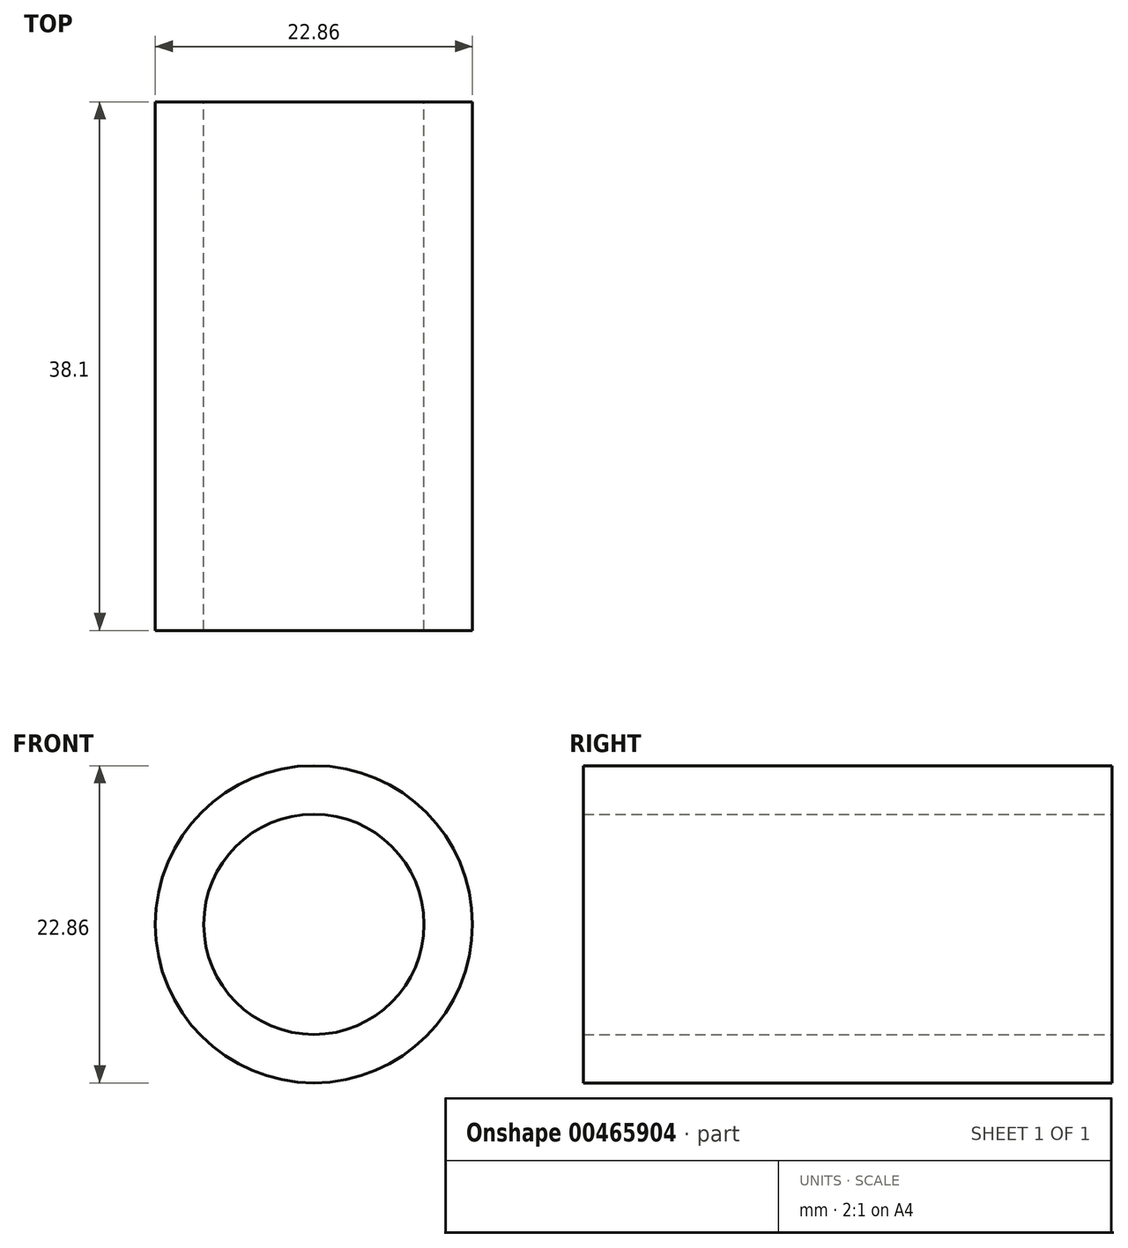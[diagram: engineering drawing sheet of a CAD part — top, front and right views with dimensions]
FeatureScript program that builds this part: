
annotation { "Feature Type Name" : "Feature", "Feature Type Description" : "" }
export const myFeature = defineFeature(function(context is Context, id is Id, definition is map)
    precondition{}
    {
        {
            var Q0;
            Q0=qCreatedBy(makeId("Front.planeOp"),FACE);
            var sketch = newSketch(context, id + "F0", { "sketchPlane" : qUnion([Q0])});
            skCircle(sketch, "E0", {"center": v(0, 0) * mm, "radius": 7.94 * mm});
            skCircle(sketch, "E1", {"center": v(0, 0) * mm, "radius": 11.43 * mm});
            skSolve(sketch);
        }
        {
            var Q0;
            Q0=makeQuery(id+"F0.imprint","IMPRINT",FACE,{"disambiguationData":[TD([[makeQuery(id+"F0.imprint","IMPRINT",EDGE,{"derivedFrom":sQuery(id+"F0.wireOp",EDGE,"E0")}),-1.0]])]});
            extrude(context, id + "F1", {"entities" : qUnion([Q0]), "depth" : 38.1 * mm});
        }
    });
